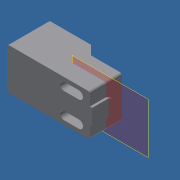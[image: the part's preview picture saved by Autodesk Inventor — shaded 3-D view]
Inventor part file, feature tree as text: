
AUTODESK INVENTOR PART (.ipt)
format: ipt  version: 2018 (Build 220112000, 112)  size: 171,520 bytes
history: native  units: mm
features: other x4, plane x1
ambient origin geometry x8: Origin, YZ Plane, XZ Plane, XY Plane, X Axis, Y Axis, Z Axis, Center Point
bodies: Solid1 (feature_tree)
feature tree (5):
  plane  "Work Plane1"
  other  "Âûðåç-Âûòÿíóòü3"
  other  "<userpath>\OneDrive\Objet3D\3DPrinter\3DPrinterBeltCoreXY.iam"
  other  "3DPrinterBeltCoreXY.iam"
  other  "HotendMountCarriage:1"
